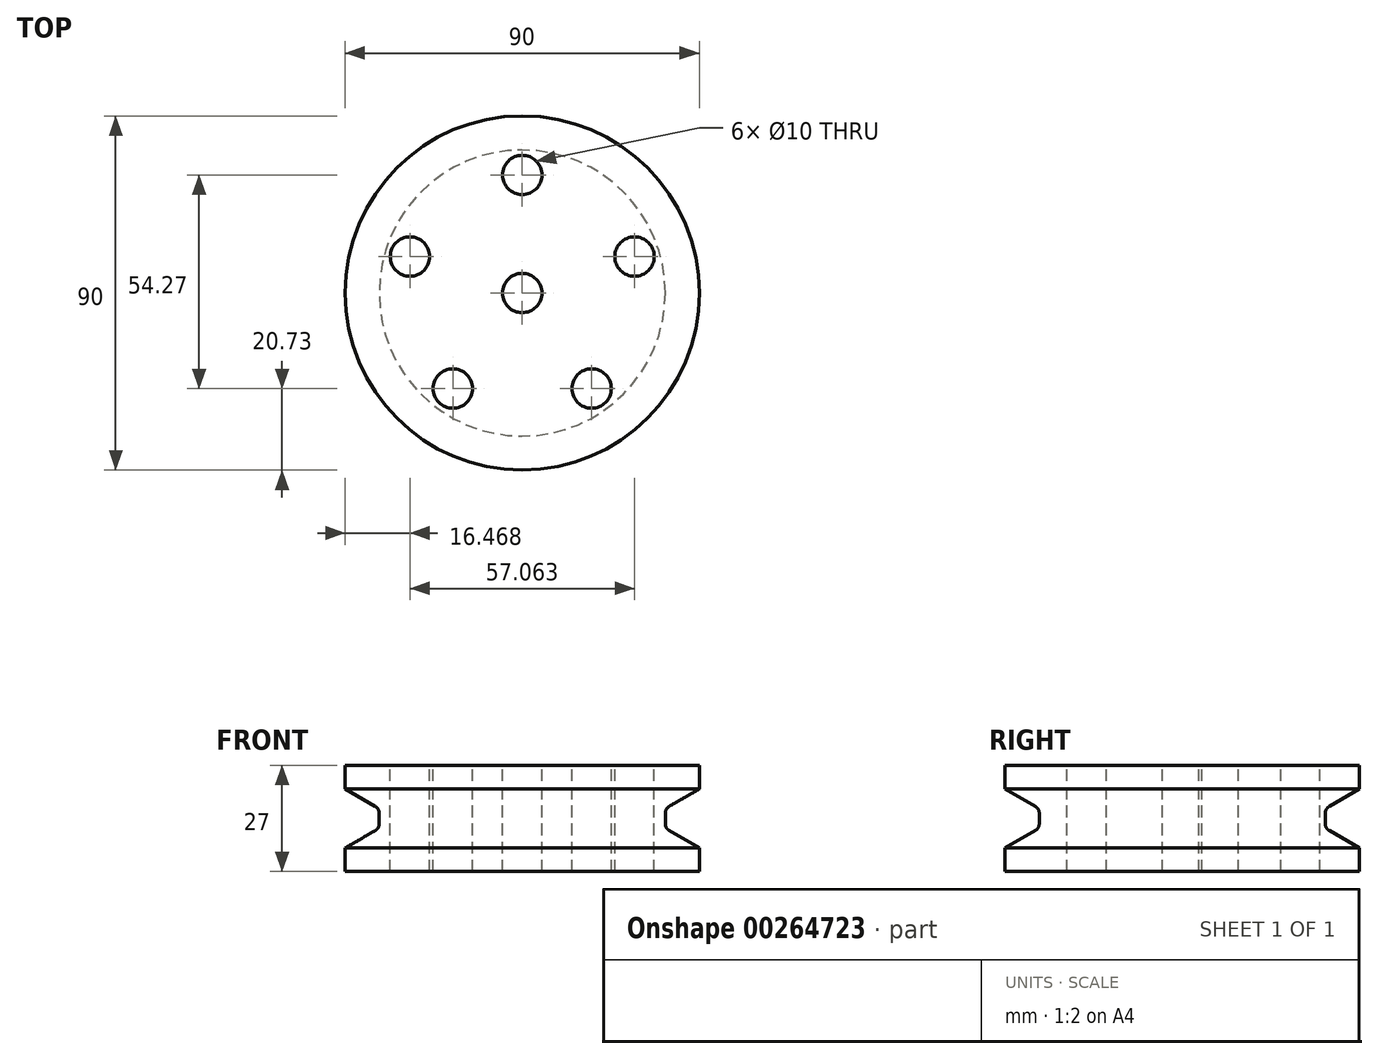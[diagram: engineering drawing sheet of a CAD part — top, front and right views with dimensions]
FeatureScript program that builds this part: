
annotation { "Feature Type Name" : "Feature", "Feature Type Description" : "" }
export const myFeature = defineFeature(function(context is Context, id is Id, definition is map)
    precondition{}
    {
        {
            var Q0;
            Q0=qCreatedBy(makeId("Right.planeOp"),FACE);
            var sketch = newSketch(context, id + "F0", { "sketchPlane" : qUnion([Q0])});
            skLineSegment(sketch, "E0", {"start": v(0, 18.74) * mm, "end": v(0, -19.73) * mm, "construction": true});
            skLineSegment(sketch, "E1", {"start": v(-5, 16) * mm, "end": v(-45, 16) * mm});
            skLineSegment(sketch, "E2", {"start": v(-45, 16) * mm, "end": v(-45, 10) * mm});
            skLineSegment(sketch, "E3", {"start": v(-45, 10) * mm, "end": v(-36.34, 5) * mm});
            skLineSegment(sketch, "E4", {"start": v(-36.34, 5) * mm, "end": v(-36.34, 0) * mm});
            skLineSegment(sketch, "E5", {"start": v(-36.34, 0) * mm, "end": v(-45, -5) * mm});
            skLineSegment(sketch, "E6", {"start": v(-45, -5) * mm, "end": v(-45, -11) * mm});
            skLineSegment(sketch, "E7", {"start": v(-45, -11) * mm, "end": v(-5, -11) * mm});
            skLineSegment(sketch, "E8", {"start": v(-5, -11) * mm, "end": v(-5, 16) * mm});
            skSolve(sketch);
        }
        {
            var Q0;
            Q0=makeQuery(id+"F0.imprint","IMPRINT",FACE,{"disambiguationData":[TD([[makeQuery(id+"F0.imprint","IMPRINT",EDGE,{"derivedFrom":sQuery(id+"F0.wireOp",EDGE,"E1")}),1.0]])]});
            var Q1;
            Q1 = qSketchRegion(id + "F2", true);
            var Q2;
            Q2=sQuery(id+"F0.wireOp",EDGE,"E0");
            revolve(context, id + "F1", {"entities" : qUnion([Q0, Q1]), "axis" : qUnion([Q2]), "revolveType" : RevolveType.FULL});
        }
        {
            var Q0;
            Q0=makeQuery(id+"F1.opRevolve","SWEPT_FACE",FACE,{"disambiguationData":[OSD([sQuery(id+"F0.wireOp",EDGE,"E1")])]});
            var sketch = newSketch(context, id + "F2", { "sketchPlane" : qUnion([Q0])});
            skCircle(sketch, "E9", {"center": v(0, 30) * mm, "radius": 5 * mm});
            skCircle(sketch, "E10.1.0", {"center": v(-28.53, 9.27) * mm, "radius": 5 * mm});
            skCircle(sketch, "E10.2.0", {"center": v(-17.63, -24.27) * mm, "radius": 5 * mm});
            skCircle(sketch, "E10.3.0", {"center": v(17.63, -24.27) * mm, "radius": 5 * mm});
            skCircle(sketch, "E10.4.0", {"center": v(28.53, 9.27) * mm, "radius": 5 * mm});
            skPoint(sketch, "E10.center", {"position": v(0, 0) * mm});
            skSolve(sketch);
        }
        {
            var Q0;
            Q0=makeQuery(id+"F2.imprint","IMPRINT",FACE,{"disambiguationData":[TD([[makeQuery(id+"F2.imprint","IMPRINT",EDGE,{"derivedFrom":sQuery(id+"F2.wireOp",EDGE,"E10.1.0")}),1.0]])]});
            var Q1;
            Q1=makeQuery(id+"F2.imprint","IMPRINT",FACE,{"disambiguationData":[TD([[makeQuery(id+"F2.imprint","IMPRINT",EDGE,{"derivedFrom":sQuery(id+"F2.wireOp",EDGE,"E10.2.0")}),1.0]])]});
            var Q2;
            Q2=makeQuery(id+"F2.imprint","IMPRINT",FACE,{"disambiguationData":[TD([[makeQuery(id+"F2.imprint","IMPRINT",EDGE,{"derivedFrom":sQuery(id+"F2.wireOp",EDGE,"E10.3.0")}),1.0]])]});
            var Q3;
            Q3=makeQuery(id+"F2.imprint","IMPRINT",FACE,{"disambiguationData":[TD([[makeQuery(id+"F2.imprint","IMPRINT",EDGE,{"derivedFrom":sQuery(id+"F2.wireOp",EDGE,"E10.4.0")}),1.0]])]});
            var Q4;
            Q4=makeQuery(id+"F2.imprint","IMPRINT",FACE,{"disambiguationData":[TD([[makeQuery(id+"F2.imprint","IMPRINT",EDGE,{"derivedFrom":sQuery(id+"F2.wireOp",EDGE,"E9")}),1.0]])]});
            var Q5;
            Q5=sQuery(id+"F2.wireOp",EDGE,"E10.1.0");
            var Q6;
            Q6=sQuery(id+"F2.wireOp",EDGE,"E9");
            var Q7;
            Q7=sQuery(id+"F2.wireOp",EDGE,"E10.4.0");
            var Q8;
            Q8=sQuery(id+"F2.wireOp",EDGE,"E10.3.0");
            var Q9;
            Q9=sQuery(id+"F2.wireOp",EDGE,"E10.2.0");
            extrude(context, id + "F3", {"entities" : qUnion([Q0, Q1, Q2, Q3, Q4]), "operationType" : NewBodyOperationType.REMOVE, "surfaceEntities" : qUnion([Q5, Q6, Q7, Q8, Q9]), "endBound" : BoundingType.UP_TO_NEXT, "oppositeDirection" : true, "depth" : 25 * mm});
        }
        {
            var Q0;
            Q0=makeQuery(id+"F1.opRevolve","SWEPT_EDGE",EDGE,{"disambiguationData":[OSD([sQuery(id+"F0.wireOp",EDGE,"E4"),sQuery(id+"F0.wireOp",EDGE,"E5")])]});
            var Q1;
            Q1=makeQuery(id+"F1.opRevolve","SWEPT_EDGE",EDGE,{"disambiguationData":[OSD([sQuery(id+"F0.wireOp",EDGE,"E3"),sQuery(id+"F0.wireOp",EDGE,"E4")])]});
            fillet(context, id + "F4", {"entities" : qUnion([Q0, Q1]), "radius" : 2 * mm, "tangentPropagation" : true, "allowEdgeOverflow" : false});
        }
    });
